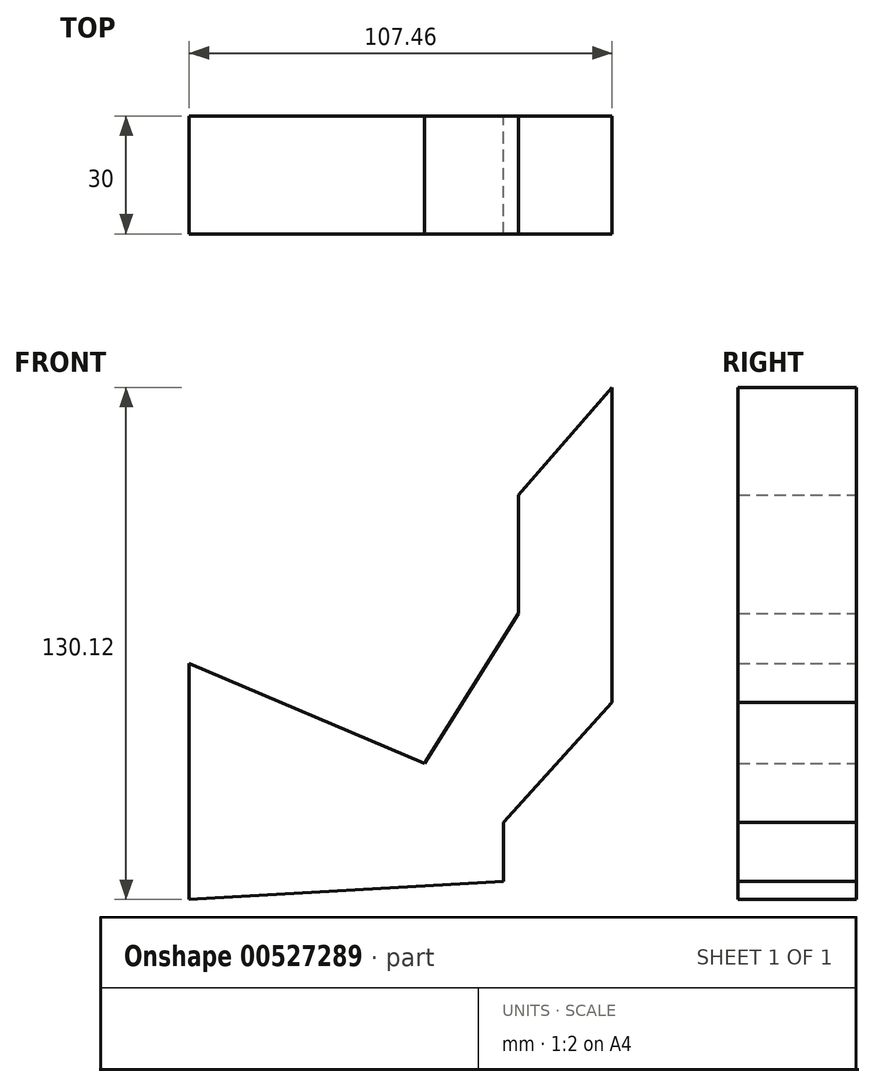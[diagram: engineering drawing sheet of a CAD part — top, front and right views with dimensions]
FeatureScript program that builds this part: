
annotation { "Feature Type Name" : "Feature", "Feature Type Description" : "" }
export const myFeature = defineFeature(function(context is Context, id is Id, definition is map)
    precondition{}
    {
        {
            var Q0;
            Q0=qCreatedBy(makeId("Front.planeOp"),FACE);
            var sketch = newSketch(context, id + "F0", { "sketchPlane" : qUnion([Q0])});
            skLineSegment(sketch, "E0", {"start": v(-295.3, 17.8) * mm, "end": v(-295.3, -42.2) * mm});
            skLineSegment(sketch, "E1", {"start": v(-295.3, 17.8) * mm, "end": v(-235.47, -7.59) * mm});
            skLineSegment(sketch, "E2", {"start": v(-235.47, -7.59) * mm, "end": v(-211.62, 30.57) * mm});
            skLineSegment(sketch, "E3", {"start": v(-211.62, 30.57) * mm, "end": v(-211.62, 60.57) * mm});
            skLineSegment(sketch, "E4", {"start": v(-211.62, 60.57) * mm, "end": v(-187.84, 87.93) * mm});
            skLineSegment(sketch, "E5", {"start": v(-187.84, 87.93) * mm, "end": v(-187.84, 7.93) * mm});
            skLineSegment(sketch, "E6", {"start": v(-215.43, -22.6) * mm, "end": v(-215.43, -37.6) * mm});
            skLineSegment(sketch, "E7", {"start": v(-215.43, -37.6) * mm, "end": v(-295.3, -42.2) * mm});
            skLineSegment(sketch, "E8", {"start": v(-215.43, -22.6) * mm, "end": v(-187.84, 7.93) * mm});
            skLineSegment(sketch, "E9", {"start": v(-211.62, 30.57) * mm, "end": v(-215.43, -22.6) * mm, "construction": true});
            skSolve(sketch);
        }
        {
            var Q0;
            Q0 = qSketchRegion(id + "F0", true);
            extrude(context, id + "F1", {"entities" : qUnion([Q0]), "depth" : 30 * mm, "offsetDistance" : 25 * mm});
        }
    });
